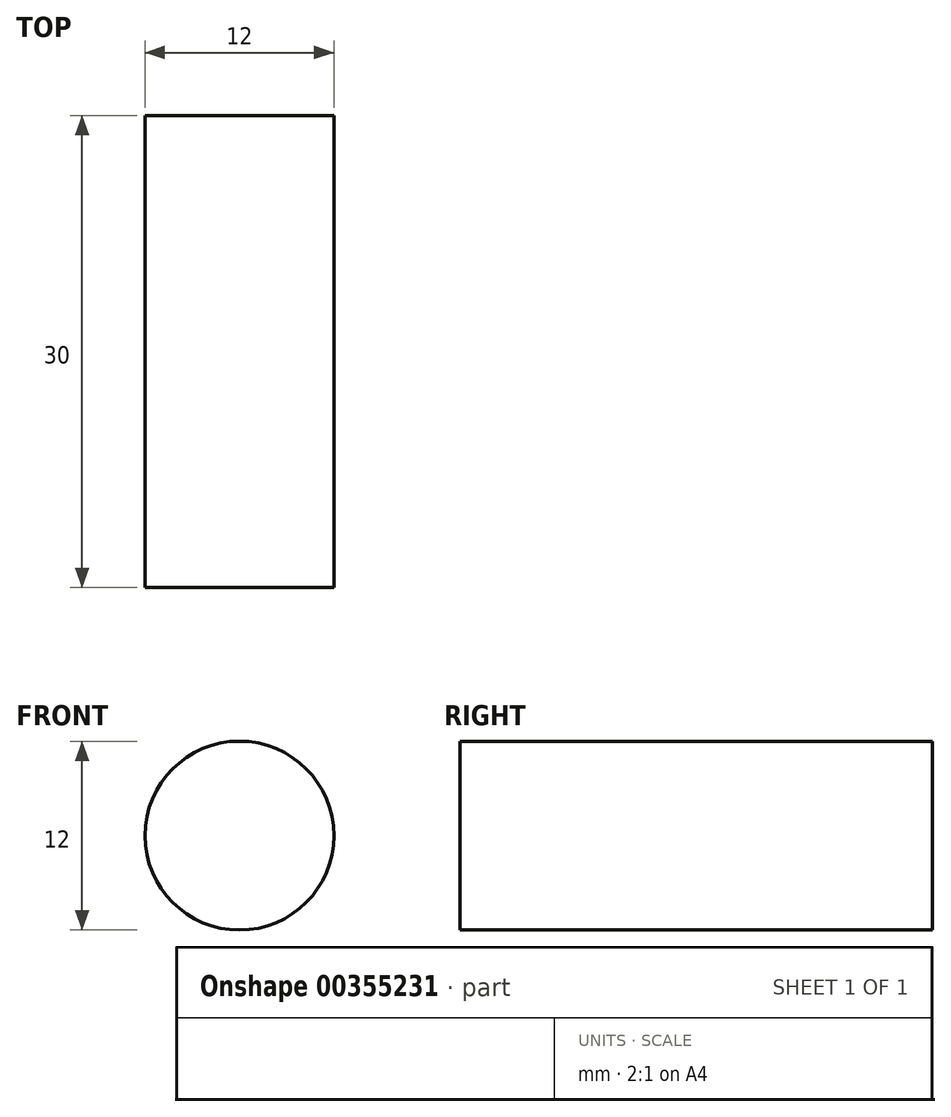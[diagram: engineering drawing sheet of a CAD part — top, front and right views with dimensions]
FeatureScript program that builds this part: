
annotation { "Feature Type Name" : "Feature", "Feature Type Description" : "" }
export const myFeature = defineFeature(function(context is Context, id is Id, definition is map)
    precondition{}
    {
        {
            var Q0;
            Q0=qCreatedBy(makeId("Front.planeOp"),FACE);
            var sketch = newSketch(context, id + "F0", { "sketchPlane" : qUnion([Q0])});
            skCircle(sketch, "E0", {"center": v(0, 0) * mm, "radius": 6 * mm});
            skSolve(sketch);
        }
        {
            var Q0;
            Q0=sQuery(id+"F0.wireOp",EDGE,"E0");
            extrude(context, id + "F1", {"bodyType" : ToolBodyType.SURFACE, "surfaceEntities" : qUnion([Q0]), "depth" : 30 * mm});
        }
    });
